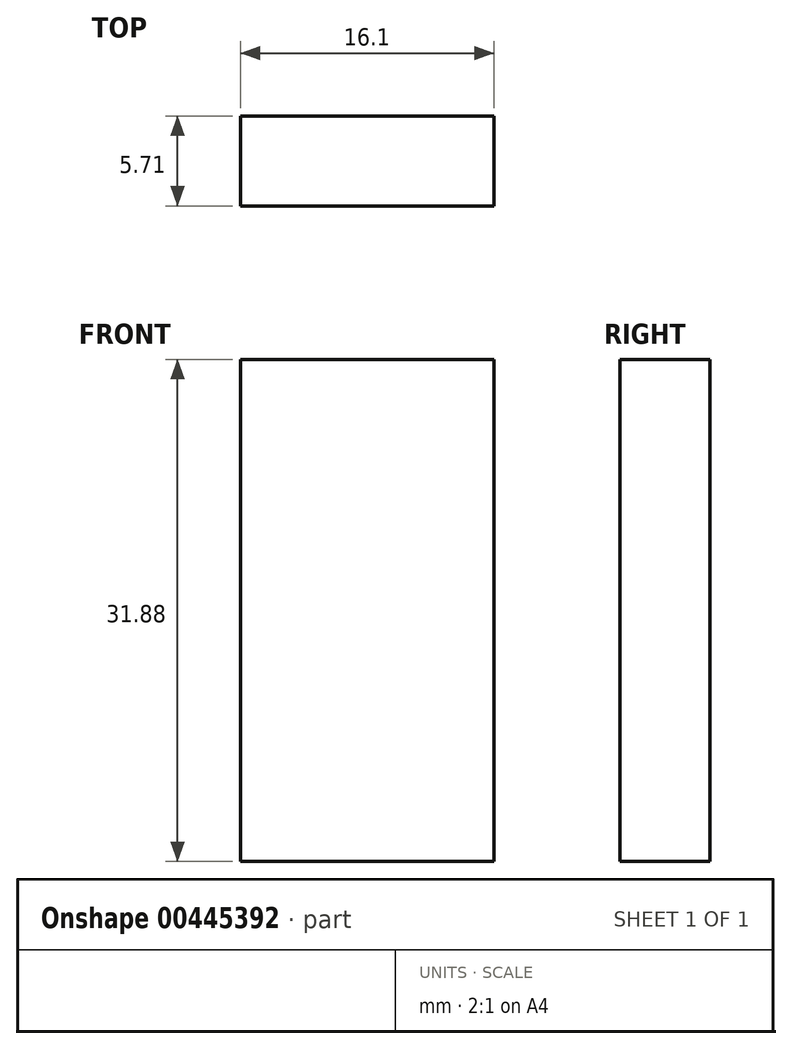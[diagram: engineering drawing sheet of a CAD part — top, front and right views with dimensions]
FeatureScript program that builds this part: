
annotation { "Feature Type Name" : "Feature", "Feature Type Description" : "" }
export const myFeature = defineFeature(function(context is Context, id is Id, definition is map)
    precondition{}
    {
        {
            var Q0;
            Q0=qCreatedBy(makeId("Front.planeOp"),FACE);
            var sketch = newSketch(context, id + "F0", { "sketchPlane" : qUnion([Q0])});
            skLineSegment(sketch, "E0", {"start": v(-21.36, -3.87) * mm, "end": v(-21.36, -35.75) * mm});
            skLineSegment(sketch, "E1", {"start": v(-21.36, -3.87) * mm, "end": v(-5.26, -3.87) * mm});
            skLineSegment(sketch, "E2", {"start": v(-5.26, -3.87) * mm, "end": v(-5.26, -35.75) * mm});
            skLineSegment(sketch, "E3", {"start": v(-5.26, -35.75) * mm, "end": v(-21.36, -35.75) * mm});
            skSolve(sketch);
        }
        {
            var Q0;
            Q0 = qSketchRegion(id + "F0", true);
            var Q1;
            Q1=makeQuery(id+"F0.imprint","IMPRINT",FACE,{"disambiguationData":[TD([[makeQuery(id+"F0.imprint","IMPRINT",EDGE,{"derivedFrom":sQuery(id+"F0.wireOp",EDGE,"E0")}),1.0]])]});
            extrude(context, id + "F1", {"entities" : qUnion([Q0, Q1]), "depth" : 5.7 * mm});
        }
    });
